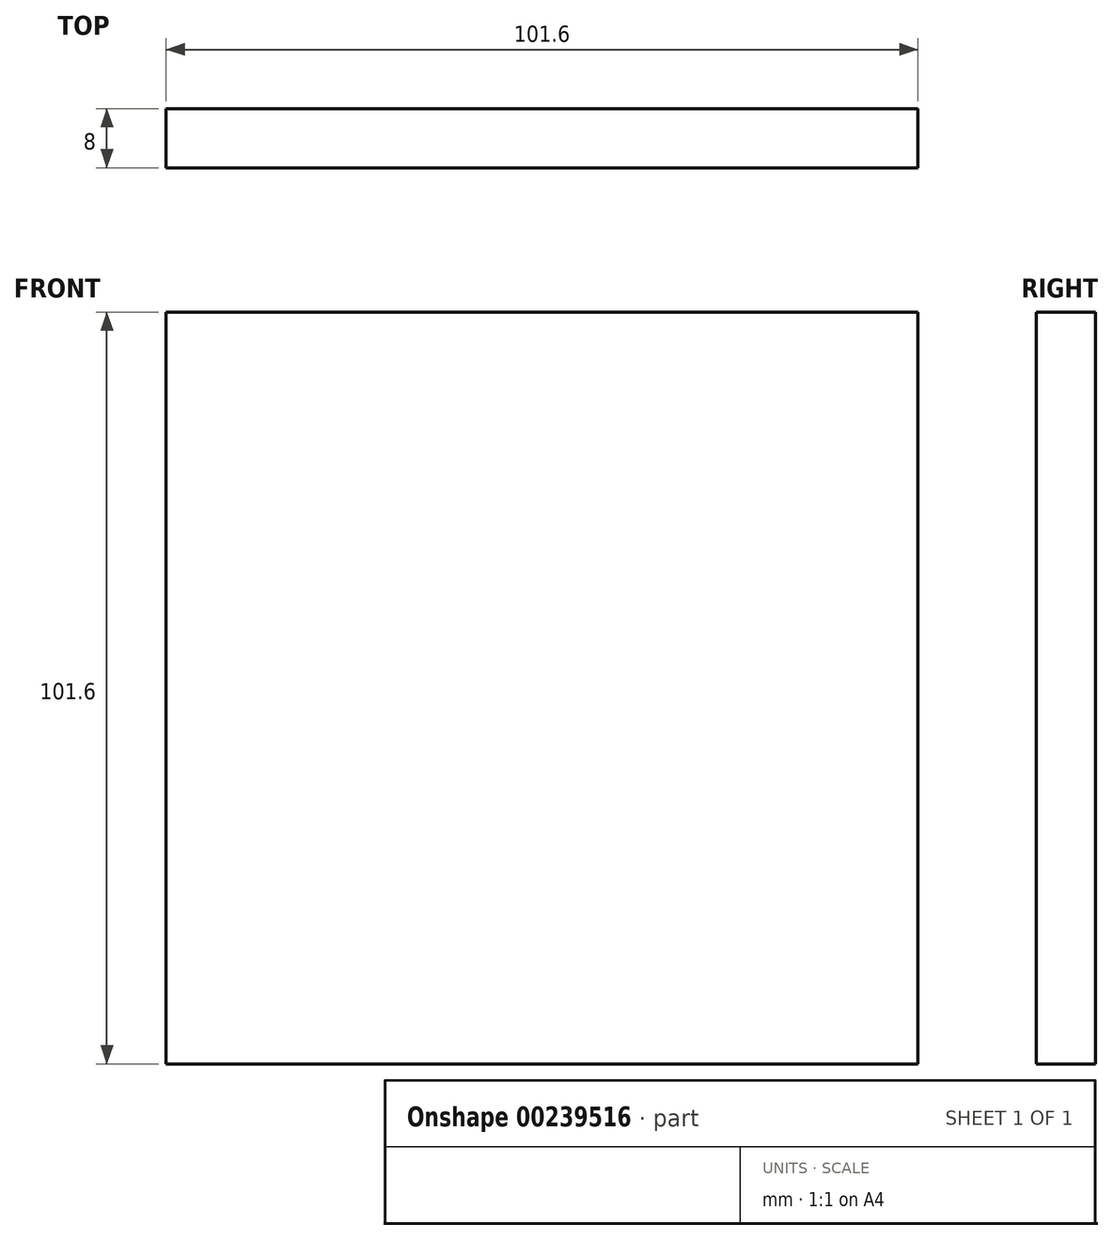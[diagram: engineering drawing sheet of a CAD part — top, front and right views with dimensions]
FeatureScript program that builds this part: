
annotation { "Feature Type Name" : "Feature", "Feature Type Description" : "" }
export const myFeature = defineFeature(function(context is Context, id is Id, definition is map)
    precondition{}
    {
        {
            assignVariable(context, id + "F0", {"name" : "P", "anyValue" : 4});
        }
        {
            var Q0;
            Q0=qCreatedBy(makeId("Front.planeOp"),FACE);
            var sketch = newSketch(context, id + "F1", { "sketchPlane" : qUnion([Q0])});
            skLineSegment(sketch, "E0.bottom", {"start": v(-50.8, 50.8) * mm, "end": v(50.8, 50.8) * mm});
            skLineSegment(sketch, "E0.top", {"start": v(-50.8, -50.8) * mm, "end": v(50.8, -50.8) * mm});
            skLineSegment(sketch, "E0.left", {"start": v(-50.8, 50.8) * mm, "end": v(-50.8, -50.8) * mm});
            skLineSegment(sketch, "E0.right", {"start": v(50.8, 50.8) * mm, "end": v(50.8, -50.8) * mm});
            skPoint(sketch, "E0.middle", {"position": v(0, 0) * mm});
            skSolve(sketch);
        }
        {
            var Q0;
            Q0 = qSketchRegion(id + "F1", true);
            extrude(context, id + "F2", {"entities" : qUnion([Q0]), "endBound" : BoundingType.SYMMETRIC, "depth" : ((getVariable(context, 'P')) * (2)) * mm});
        }
    });
